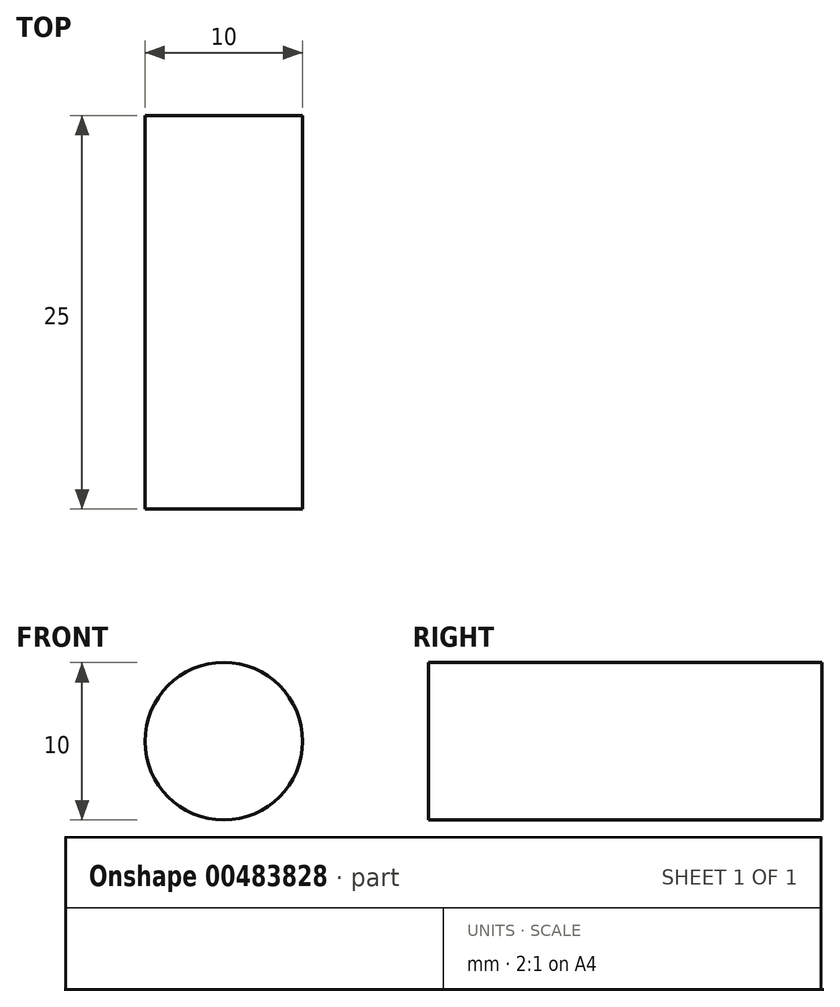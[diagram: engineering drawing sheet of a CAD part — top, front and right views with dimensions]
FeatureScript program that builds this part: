
annotation { "Feature Type Name" : "Feature", "Feature Type Description" : "" }
export const myFeature = defineFeature(function(context is Context, id is Id, definition is map)
    precondition{}
    {
        {
            var Q0;
            Q0=qCreatedBy(makeId("Front.planeOp"),FACE);
            var sketch = newSketch(context, id + "F0", { "sketchPlane" : qUnion([Q0])});
            skCircle(sketch, "E0", {"center": v(-5.83, 6.25) * mm, "radius": 5 * mm});
            skSolve(sketch);
        }
        {
            var Q0;
            Q0=makeQuery(id+"F0.imprint","IMPRINT",FACE,{"disambiguationData":[TD([[makeQuery(id+"F0.imprint","IMPRINT",EDGE,{"derivedFrom":sQuery(id+"F0.wireOp",EDGE,"E0")}),1.0]])]});
            extrude(context, id + "F1", {"entities" : qUnion([Q0]), "depth" : 25 * mm});
        }
    });
